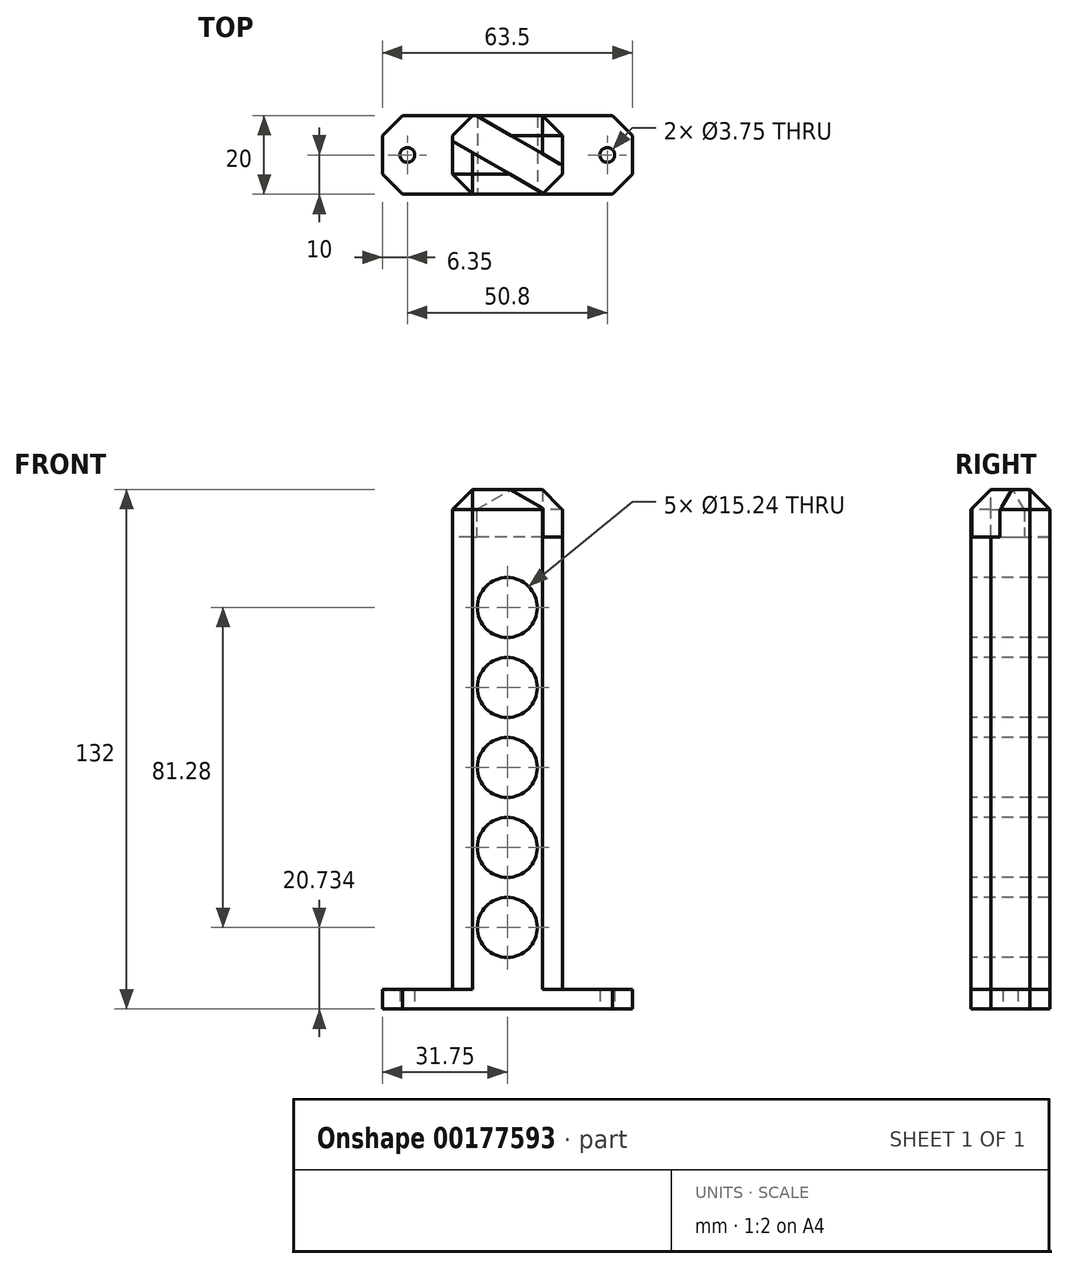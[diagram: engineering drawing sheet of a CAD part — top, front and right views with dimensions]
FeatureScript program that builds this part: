
annotation { "Feature Type Name" : "Feature", "Feature Type Description" : "" }
export const myFeature = defineFeature(function(context is Context, id is Id, definition is map)
    precondition{}
    {
        {
            var Q0;
            Q0=qCreatedBy(makeId("Top.planeOp"),FACE);
            var sketch = newSketch(context, id + "F0", { "sketchPlane" : qUnion([Q0])});
            skLineSegment(sketch, "E0.bottom", {"start": v(-31.75, 10) * mm, "end": v(31.75, 10) * mm});
            skLineSegment(sketch, "E0.top", {"start": v(-31.75, -10) * mm, "end": v(31.75, -10) * mm});
            skLineSegment(sketch, "E0.left", {"start": v(-31.75, 10) * mm, "end": v(-31.75, -10) * mm});
            skLineSegment(sketch, "E0.right", {"start": v(31.75, 10) * mm, "end": v(31.75, -10) * mm});
            skCircle(sketch, "E1", {"center": v(-25.4, 0) * mm, "radius": 1.88 * mm});
            skCircle(sketch, "E2", {"center": v(25.4, 0) * mm, "radius": 1.88 * mm});
            skSolve(sketch);
        }
        {
            var Q0;
            Q0 = qSketchRegion(id + "F0", true);
            extrude(context, id + "F1", {"entities" : qUnion([Q0]), "depth" : 5 * mm});
        }
        {
            var Q0;
            Q0=makeQuery(id+"F1.opExtrude","CAP_FACE",FACE,{"disambiguationData":[OSD([sQuery(id+"F0.wireOp",EDGE,"E0.bottom"),sQuery(id+"F0.wireOp",EDGE,"E0.top"),sQuery(id+"F0.wireOp",EDGE,"E0.left"),sQuery(id+"F0.wireOp",EDGE,"E0.right"),sQuery(id+"F0.wireOp",EDGE,"uP7g0JNC-KzfL-0Rti-bCjR-gVSRn8DtXRZG"),sQuery(id+"F0.wireOp",EDGE,"p9lesepK-KzLN-vSE6-c4vS-AvBVuWL7il3u")])],"isStart":false});
            var sketch = newSketch(context, id + "F2", { "sketchPlane" : qUnion([Q0])});
            skLineSegment(sketch, "E3.bottom", {"start": v(13.97, -10) * mm, "end": v(-13.97, -10) * mm});
            skLineSegment(sketch, "E3.top", {"start": v(13.97, 10) * mm, "end": v(-13.97, 10) * mm});
            skLineSegment(sketch, "E3.left", {"start": v(13.97, -10) * mm, "end": v(13.97, 10) * mm});
            skLineSegment(sketch, "E3.right", {"start": v(-13.97, -10) * mm, "end": v(-13.97, 10) * mm});
            skPoint(sketch, "E3.middle", {"position": v(0, 0) * mm});
            skSolve(sketch);
        }
        {
            var Q0;
            Q0=makeQuery(id+"F2.imprint","IMPRINT",FACE,{"disambiguationData":[TD([[makeQuery(id+"F2.imprint","IMPRINT",EDGE,{"derivedFrom":sQuery(id+"F2.wireOp",EDGE,"E3.bottom")}),1.0]])]});
            extrude(context, id + "F3", {"entities" : qUnion([Q0]), "operationType" : NewBodyOperationType.ADD, "depth" : 127 * mm});
        }
        {
            var Q0;
            Q0=makeQuery(id+"F3.boolean.opBoolean","MERGE",FACE,{"derivedFrom":[makeQuery(id+"F1.opExtrude","SWEPT_FACE",FACE,{"disambiguationData":[OSD([sQuery(id+"F0.wireOp",EDGE,"E0.top")])]}),makeQuery(id+"F3.opExtrude","SWEPT_FACE",FACE,{"disambiguationData":[OSD([sQuery(id+"F2.wireOp",EDGE,"E3.bottom")])]})]});
            var sketch = newSketch(context, id + "F4", { "sketchPlane" : qUnion([Q0])});
            skCircle(sketch, "E4", {"center": v(0, 20.73) * mm, "radius": 7.62 * mm});
            skCircle(sketch, "E5.0.1.0", {"center": v(0, 41.05) * mm, "radius": 7.62 * mm});
            skCircle(sketch, "E5.0.2.0", {"center": v(0, 61.37) * mm, "radius": 7.62 * mm});
            skCircle(sketch, "E5.0.3.0", {"center": v(0, 81.7) * mm, "radius": 7.62 * mm});
            skCircle(sketch, "E5.0.4.0", {"center": v(0, 102.01) * mm, "radius": 7.62 * mm});
            skLineSegment(sketch, "E5.direction2", {"start": v(0, 20.73) * mm, "end": v(0, 41.05) * mm, "construction": true});
            skLineSegment(sketch, "E6", {"start": v(0, 41.05) * mm, "end": v(0, 61.37) * mm, "construction": true});
            skLineSegment(sketch, "E7", {"start": v(0, 61.37) * mm, "end": v(0, 81.7) * mm, "construction": true});
            skLineSegment(sketch, "E8", {"start": v(0, 81.7) * mm, "end": v(0, 102.01) * mm, "construction": true});
            skSolve(sketch);
        }
        {
            var Q0;
            Q0=makeQuery(id+"F4.imprint","IMPRINT",FACE,{"disambiguationData":[TD([[makeQuery(id+"F4.imprint","IMPRINT",EDGE,{"derivedFrom":sQuery(id+"F4.wireOp",EDGE,"E5.0.4.0")}),1.0]])]});
            var Q1;
            Q1=makeQuery(id+"F4.imprint","IMPRINT",FACE,{"disambiguationData":[TD([[makeQuery(id+"F4.imprint","IMPRINT",EDGE,{"derivedFrom":sQuery(id+"F4.wireOp",EDGE,"E5.0.3.0")}),1.0]])]});
            var Q2;
            Q2=makeQuery(id+"F4.imprint","IMPRINT",FACE,{"disambiguationData":[TD([[makeQuery(id+"F4.imprint","IMPRINT",EDGE,{"derivedFrom":sQuery(id+"F4.wireOp",EDGE,"E5.0.2.0")}),1.0]])]});
            var Q3;
            Q3=makeQuery(id+"F4.imprint","IMPRINT",FACE,{"disambiguationData":[TD([[makeQuery(id+"F4.imprint","IMPRINT",EDGE,{"derivedFrom":sQuery(id+"F4.wireOp",EDGE,"E5.0.1.0")}),1.0]])]});
            var Q4;
            Q4=makeQuery(id+"F4.imprint","IMPRINT",FACE,{"disambiguationData":[TD([[makeQuery(id+"F4.imprint","IMPRINT",EDGE,{"derivedFrom":sQuery(id+"F4.wireOp",EDGE,"E4")}),1.0]])]});
            extrude(context, id + "F5", {"entities" : qUnion([Q0, Q1, Q2, Q3, Q4]), "operationType" : NewBodyOperationType.REMOVE, "oppositeDirection" : true, "depth" : 25.4 * mm});
        }
        {
            var Q0;
            Q0=makeQuery(id+"F3.opExtrude","SWEPT_EDGE",EDGE,{"disambiguationData":[OSD([sQuery(id+"F0.wireOp",EDGE,"E0.top"),sQuery(id+"F2.wireOp",EDGE,"E3.bottom"),sQuery(id+"F2.wireOp",EDGE,"E3.right")])]});
            var Q1;
            Q1=makeQuery(id+"F3.opExtrude","SWEPT_EDGE",EDGE,{"disambiguationData":[OSD([sQuery(id+"F0.wireOp",EDGE,"E0.top"),sQuery(id+"F2.wireOp",EDGE,"E3.bottom"),sQuery(id+"F2.wireOp",EDGE,"E3.left")])]});
            var Q2;
            Q2=makeQuery(id+"F3.opExtrude","SWEPT_EDGE",EDGE,{"disambiguationData":[OSD([sQuery(id+"F0.wireOp",EDGE,"E0.bottom"),sQuery(id+"F2.wireOp",EDGE,"E3.top"),sQuery(id+"F2.wireOp",EDGE,"E3.left")])]});
            var Q3;
            Q3=makeQuery(id+"F3.opExtrude","SWEPT_EDGE",EDGE,{"disambiguationData":[OSD([sQuery(id+"F0.wireOp",EDGE,"E0.bottom"),sQuery(id+"F2.wireOp",EDGE,"E3.top"),sQuery(id+"F2.wireOp",EDGE,"E3.right")])]});
            var Q4;
            Q4=makeQuery(id+"F3.opExtrude","CAP_EDGE",EDGE,{"disambiguationData":[OSD([sQuery(id+"F2.wireOp",EDGE,"E3.right")])],"isStart":false});
            var Q5;
            Q5=makeQuery(id+"F3.opExtrude","CAP_EDGE",EDGE,{"disambiguationData":[OSD([sQuery(id+"F2.wireOp",EDGE,"E3.bottom")])],"isStart":false});
            var Q6;
            Q6=makeQuery(id+"F3.opExtrude","CAP_EDGE",EDGE,{"disambiguationData":[OSD([sQuery(id+"F2.wireOp",EDGE,"E3.left")])],"isStart":false});
            var Q7;
            Q7=makeQuery(id+"F3.opExtrude","CAP_EDGE",EDGE,{"disambiguationData":[OSD([sQuery(id+"F2.wireOp",EDGE,"E3.top")])],"isStart":false});
            var Q8;
            Q8=makeQuery(id+"F1.opExtrude","SWEPT_EDGE",EDGE,{"disambiguationData":[OSD([sQuery(id+"F0.wireOp",EDGE,"E0.top"),sQuery(id+"F0.wireOp",EDGE,"E0.left")])]});
            var Q9;
            Q9=makeQuery(id+"F1.opExtrude","SWEPT_EDGE",EDGE,{"disambiguationData":[OSD([sQuery(id+"F0.wireOp",EDGE,"E0.bottom"),sQuery(id+"F0.wireOp",EDGE,"E0.right")])]});
            var Q10;
            Q10=makeQuery(id+"F1.opExtrude","SWEPT_EDGE",EDGE,{"disambiguationData":[OSD([sQuery(id+"F0.wireOp",EDGE,"E0.top"),sQuery(id+"F0.wireOp",EDGE,"E0.right")])]});
            var Q11;
            Q11=makeQuery(id+"F1.opExtrude","SWEPT_EDGE",EDGE,{"disambiguationData":[OSD([sQuery(id+"F0.wireOp",EDGE,"E0.bottom"),sQuery(id+"F0.wireOp",EDGE,"E0.left")])]});
            chamfer(context, id + "F6", {"entities" : qUnion([Q0, Q1, Q2, Q3, Q4, Q5, Q6, Q7, Q8, Q9, Q10, Q11]), "width" : 5.08 * mm, "tangentPropagation" : true});
        }
        {
            var Q0;
            Q0=makeQuery(id+"F3.opExtrude","CAP_FACE",FACE,{"disambiguationData":[OSD([sQuery(id+"F2.wireOp",EDGE,"E3.bottom"),sQuery(id+"F2.wireOp",EDGE,"E3.top"),sQuery(id+"F2.wireOp",EDGE,"E3.left"),sQuery(id+"F2.wireOp",EDGE,"E3.right")])],"isStart":false});
            var sketch = newSketch(context, id + "F7", { "sketchPlane" : qUnion([Q0])});
            skLineSegment(sketch, "E9", {"start": v(11.29, -6.02) * mm, "end": v(-12.17, 7.52) * mm});
            skArc(sketch, "E10.0.startCap", {"start": v(13.45, -2.27) * mm, "mid": v(15.03, -8.18) * mm, "end": v(9.12, -9.76) * mm});
            skArc(sketch, "E10.0.endCap", {"start": v(-14.33, 3.78) * mm, "mid": v(-15.91, 9.69) * mm, "end": v(-10, 11.27) * mm});
            skLineSegment(sketch, "E10.0.left", {"start": v(9.12, -9.76) * mm, "end": v(-14.33, 3.78) * mm});
            skLineSegment(sketch, "E10.0.right", {"start": v(13.45, -2.27) * mm, "end": v(-10, 11.27) * mm});
            skSolve(sketch);
        }
        {
            var Q0;
            Q0 = qSketchRegion(id + "F7", true);
            extrude(context, id + "F8", {"entities" : qUnion([Q0]), "operationType" : NewBodyOperationType.REMOVE, "oppositeDirection" : true, "depth" : 12 * mm});
        }
    });
